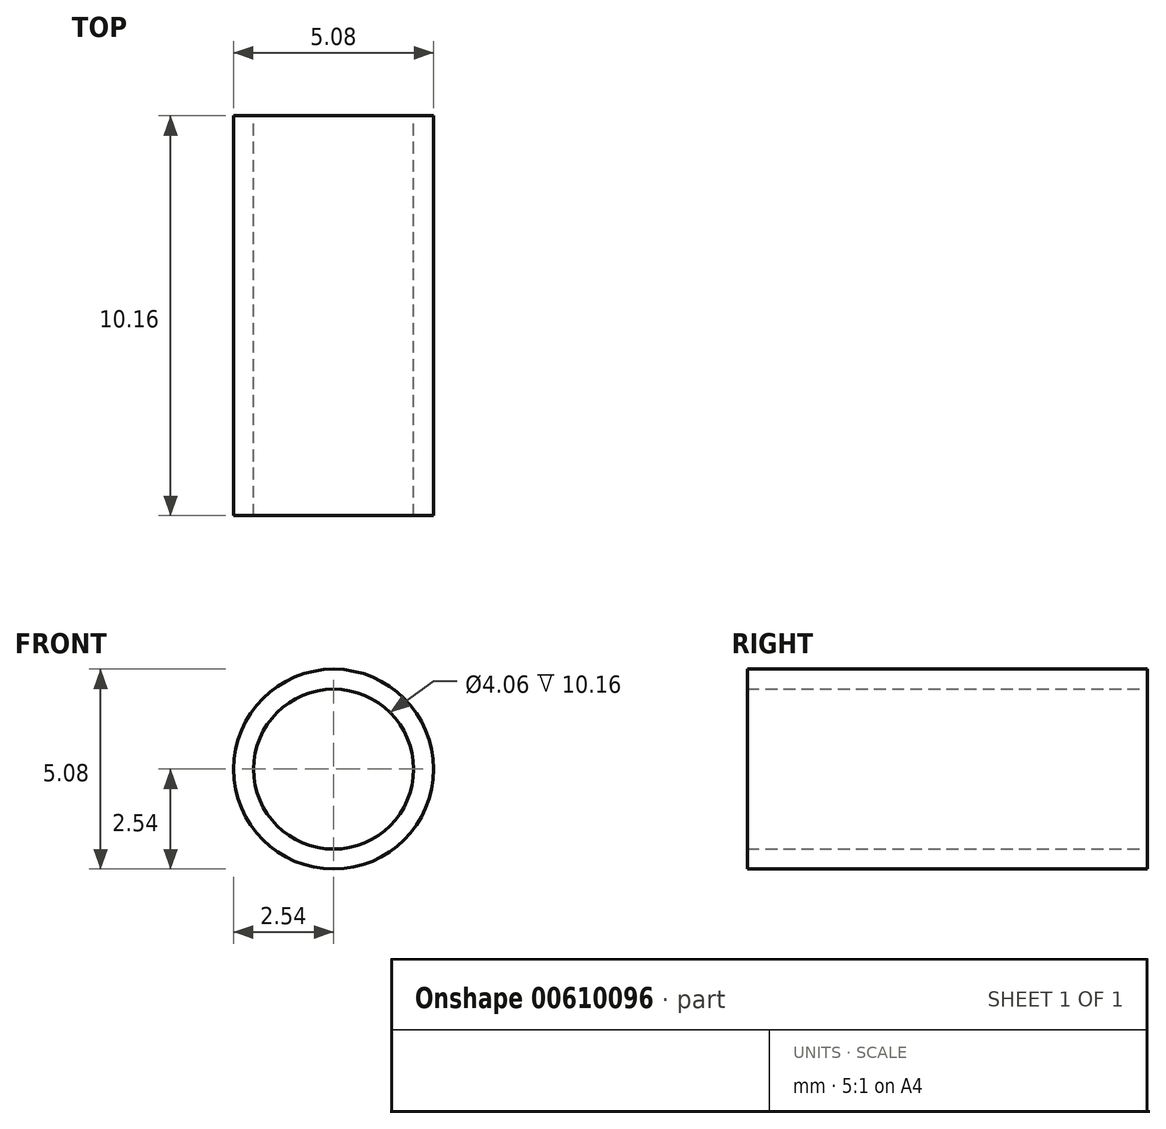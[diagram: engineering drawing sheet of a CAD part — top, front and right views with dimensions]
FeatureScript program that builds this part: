
annotation { "Feature Type Name" : "Feature", "Feature Type Description" : "" }
export const myFeature = defineFeature(function(context is Context, id is Id, definition is map)
    precondition{}
    {
        {
            var Q0;
            Q0=qCreatedBy(makeId("Front.planeOp"),FACE);
            var sketch = newSketch(context, id + "F0", { "sketchPlane" : qUnion([Q0])});
            skCircle(sketch, "E0", {"center": v(0, 0) * mm, "radius": 2.03 * mm});
            skCircle(sketch, "E1", {"center": v(0, 0) * mm, "radius": 2.54 * mm});
            skSolve(sketch);
        }
        {
            var Q0;
            Q0=makeQuery(id+"F0.imprint","IMPRINT",FACE,{"disambiguationData":[TD([[makeQuery(id+"F0.imprint","IMPRINT",EDGE,{"derivedFrom":sQuery(id+"F0.wireOp",EDGE,"E0")}),-1.0]])]});
            extrude(context, id + "F1", {"entities" : qUnion([Q0]), "depth" : 10.16 * mm, "offsetDistance" : 25.4 * mm});
        }
    });
